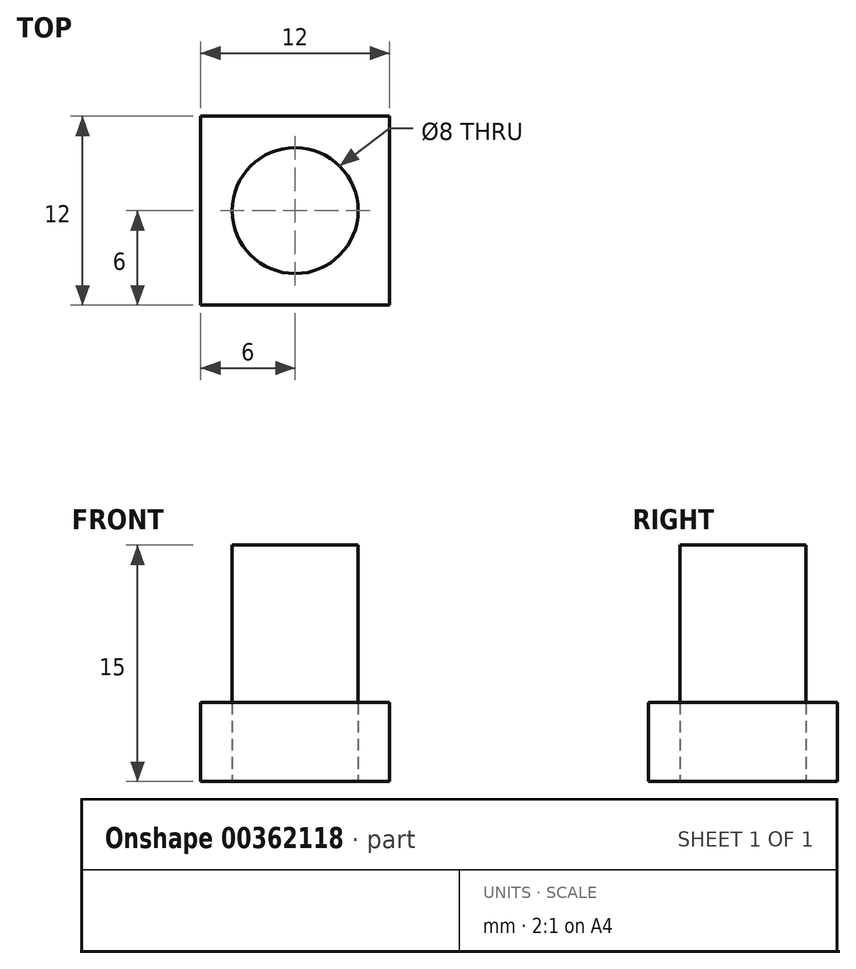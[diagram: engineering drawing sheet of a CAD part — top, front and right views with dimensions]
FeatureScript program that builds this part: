
annotation { "Feature Type Name" : "Feature", "Feature Type Description" : "" }
export const myFeature = defineFeature(function(context is Context, id is Id, definition is map)
    precondition{}
    {
        {
            var Q0;
            Q0=qCreatedBy(makeId("Top.planeOp"),FACE);
            var sketch = newSketch(context, id + "F0", { "sketchPlane" : qUnion([Q0])});
            skCircle(sketch, "E0", {"center": v(0, 0) * mm, "radius": 4 * mm});
            skLineSegment(sketch, "E1.bottom", {"start": v(-6, 6) * mm, "end": v(6, 6) * mm});
            skLineSegment(sketch, "E1.top", {"start": v(-6, -6) * mm, "end": v(6, -6) * mm});
            skLineSegment(sketch, "E1.left", {"start": v(-6, 6) * mm, "end": v(-6, -6) * mm});
            skLineSegment(sketch, "E1.right", {"start": v(6, 6) * mm, "end": v(6, -6) * mm});
            skSolve(sketch);
        }
        {
            var Q0;
            Q0=makeQuery(id+"F0.imprint","IMPRINT",FACE,{"disambiguationData":[TD([[makeQuery(id+"F0.imprint","IMPRINT",EDGE,{"derivedFrom":sQuery(id+"F0.wireOp",EDGE,"E0")}),-1.0]])]});
            extrude(context, id + "F1", {"entities" : qUnion([Q0]), "depth" : 5 * mm, "offsetDistance" : 25 * mm});
        }
        {
            var Q0;
            Q0=qCreatedBy(makeId("Top.planeOp"),FACE);
            var sketch = newSketch(context, id + "F2", { "sketchPlane" : qUnion([Q0])});
            skCircle(sketch, "E2", {"center": v(0, 0) * mm, "radius": 4 * mm});
            skSolve(sketch);
        }
        {
            var Q0;
            Q0=makeQuery(id+"F2.imprint","IMPRINT",FACE,{"disambiguationData":[TD([[makeQuery(id+"F2.imprint","IMPRINT",EDGE,{"derivedFrom":sQuery(id+"F2.wireOp",EDGE,"E2")}),1.0]])]});
            extrude(context, id + "F3", {"entities" : qUnion([Q0]), "depth" : 15 * mm, "offsetDistance" : 25 * mm});
        }
    });
